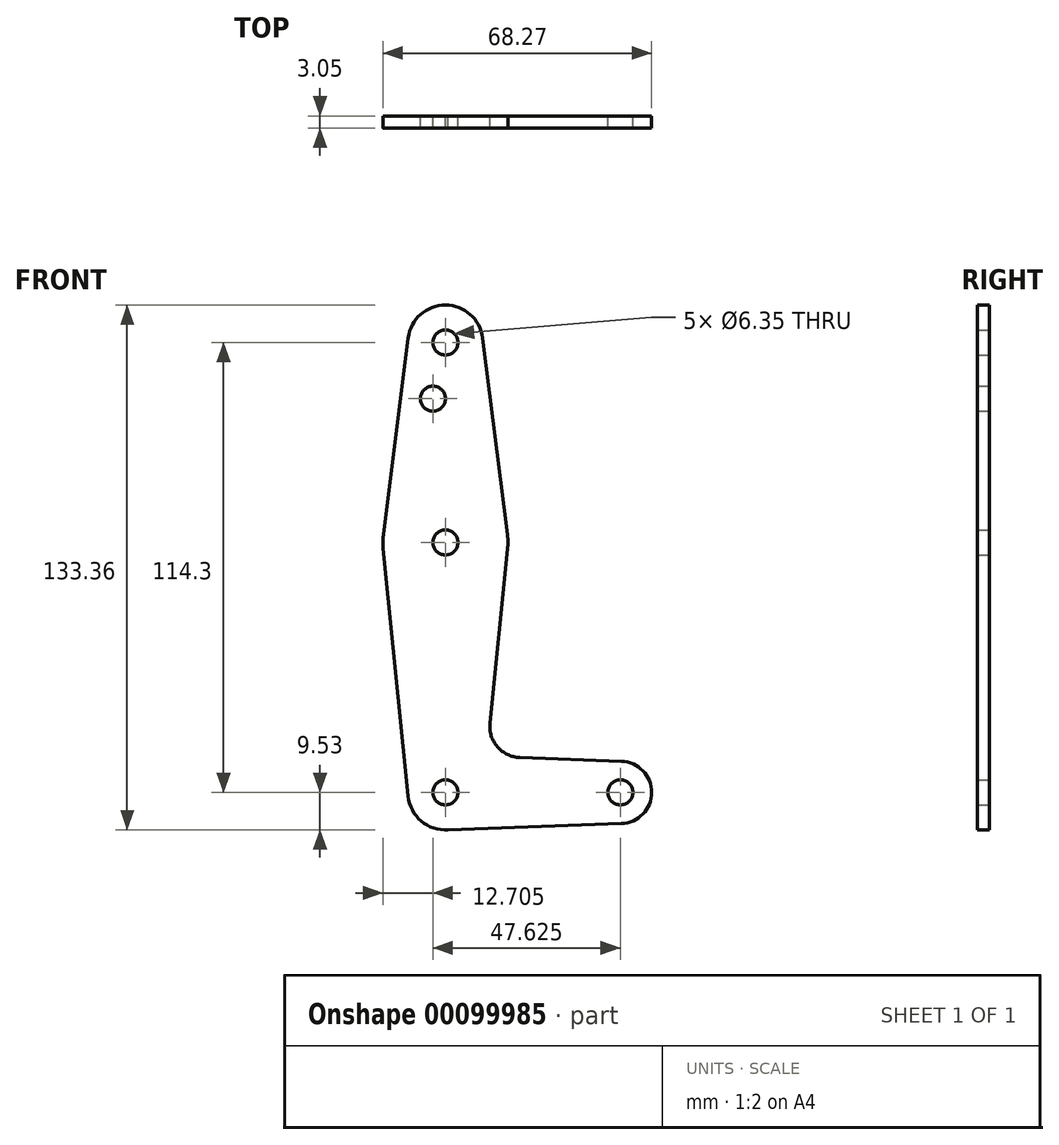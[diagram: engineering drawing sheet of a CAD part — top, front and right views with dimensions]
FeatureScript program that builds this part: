
annotation { "Feature Type Name" : "Feature", "Feature Type Description" : "" }
export const myFeature = defineFeature(function(context is Context, id is Id, definition is map)
    precondition{}
    {
        {
            var Q0;
            Q0=qCreatedBy(makeId("Front.planeOp"),FACE);
            var sketch = newSketch(context, id + "F0", { "sketchPlane" : qUnion([Q0])});
            skLineSegment(sketch, "E0", {"start": v(0, 114.3) * mm, "end": v(0, 0) * mm});
            skLineSegment(sketch, "E1", {"start": v(0, 0) * mm, "end": v(44.45, 0) * mm});
            skCircle(sketch, "E2", {"center": v(0, 114.3) * mm, "radius": 9.53 * mm});
            skCircle(sketch, "E3", {"center": v(0, 63.5) * mm, "radius": 15.88 * mm});
            skCircle(sketch, "E4", {"center": v(0, 0) * mm, "radius": 9.53 * mm});
            skCircle(sketch, "E5", {"center": v(44.45, 0) * mm, "radius": 7.94 * mm});
            skLineSegment(sketch, "E6", {"start": v(-9.45, 115.5) * mm, "end": v(-15.75, 65.48) * mm});
            skLineSegment(sketch, "E7", {"start": v(0, -9.53) * mm, "end": v(44.73, -7.93) * mm});
            skLineSegment(sketch, "E8", {"start": v(18.93, 8.85) * mm, "end": v(44.73, 7.93) * mm});
            skLineSegment(sketch, "E9", {"start": v(11.3, 17.6) * mm, "end": v(15.8, 61.9) * mm});
            skLineSegment(sketch, "E10", {"start": v(-15.8, 61.91) * mm, "end": v(-9.48, -0.95) * mm});
            skCircle(sketch, "E11", {"center": v(0, 114.3) * mm, "radius": 3.18 * mm});
            skLineSegment(sketch, "E12", {"start": v(9.45, 115.5) * mm, "end": v(15.75, 65.48) * mm});
            skCircle(sketch, "E13", {"center": v(0, 0) * mm, "radius": 3.18 * mm});
            skCircle(sketch, "E14", {"center": v(44.45, 0) * mm, "radius": 3.18 * mm});
            skCircle(sketch, "E15", {"center": v(0, 63.5) * mm, "radius": 3.18 * mm});
            skArc(sketch, "E16.filletArc", {"start": v(11.3, 17.6) * mm, "mid": v(13.22, 11.57) * mm, "end": v(18.93, 8.85) * mm});
            skCircle(sketch, "E17", {"center": v(-3.17, 100.03) * mm, "radius": 3.18 * mm});
            skSolve(sketch);
        }
        {
            var Q0;
            Q0 = qSketchRegion(id + "F0", true);
            var Q1;
            {var subQ0=sQuery(id+"F0.wireOp",EDGE,"E4");var subQ1=sQuery(id+"F0.wireOp",EDGE,"E0");var subQ2=makeQuery(id+"F0.imprint","INTERSECT",VERTEX,{"derivedFrom":[subQ1,subQ0]});Q1=makeQuery(id+"F0.imprint","IMPRINT",FACE,{"disambiguationData":[TD([[makeQuery(id+"F0.imprint","IMPRINT",EDGE,{"disambiguationData":[TD([[subQ2,-1.0]])],"derivedFrom":subQ1}),1.0]])]});}
            extrude(context, id + "F1", {"entities" : qUnion([Q0, Q1]), "depth" : 3.05 * mm});
        }
    });
